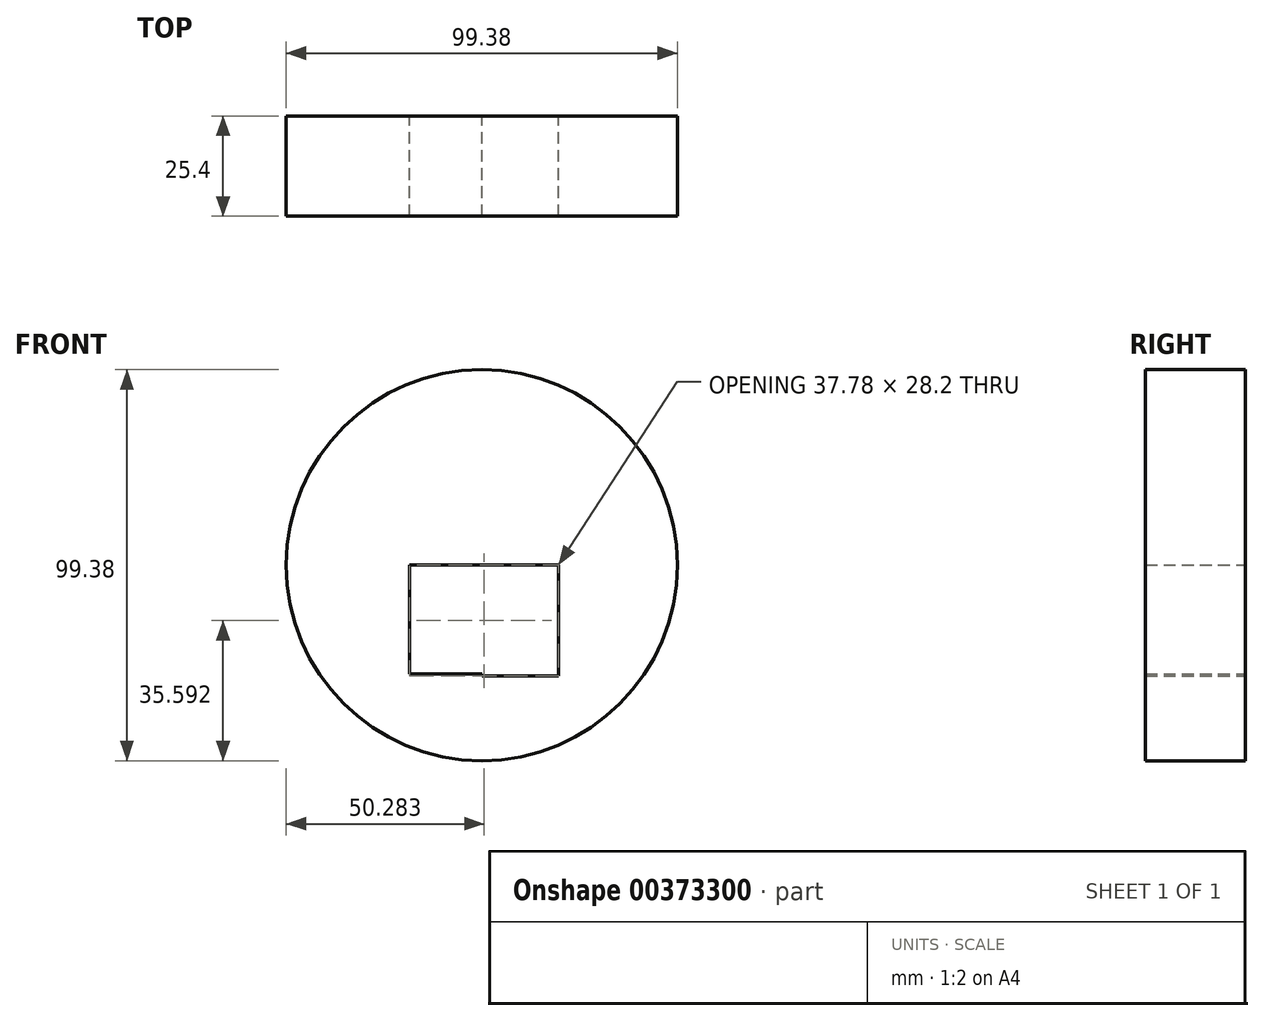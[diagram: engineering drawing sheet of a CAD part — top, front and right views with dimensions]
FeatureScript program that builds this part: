
annotation { "Feature Type Name" : "Feature", "Feature Type Description" : "" }
export const myFeature = defineFeature(function(context is Context, id is Id, definition is map)
    precondition{}
    {
        {
            var Q0;
            Q0=qCreatedBy(makeId("Front.planeOp"),FACE);
            var sketch = newSketch(context, id + "F0", { "sketchPlane" : qUnion([Q0])});
            skCircle(sketch, "E0", {"center": v(0, 0) * mm, "radius": 49.69 * mm});
            skLineSegment(sketch, "E1.bottom", {"start": v(0, 0) * mm, "end": v(19.48, 0) * mm});
            skLineSegment(sketch, "E1.top", {"start": v(0, -28.2) * mm, "end": v(19.48, -28.2) * mm});
            skLineSegment(sketch, "E1.left", {"start": v(0, 0) * mm, "end": v(0, -28.2) * mm});
            skLineSegment(sketch, "E1.right", {"start": v(19.48, 0) * mm, "end": v(19.48, -28.2) * mm});
            skLineSegment(sketch, "E2.bottom", {"start": v(0, 0) * mm, "end": v(-18.3, 0) * mm});
            skLineSegment(sketch, "E2.top", {"start": v(0, -27.65) * mm, "end": v(-18.3, -27.65) * mm});
            skLineSegment(sketch, "E2.left", {"start": v(0, 0) * mm, "end": v(0, -27.65) * mm});
            skLineSegment(sketch, "E2.right", {"start": v(-18.3, 0) * mm, "end": v(-18.3, -27.65) * mm});
            skSolve(sketch);
        }
        {
            var Q0;
            Q0 = qSketchRegion(id + "F0", true);
            extrude(context, id + "F1", {"entities" : qUnion([Q0]), "depth" : 25.4 * mm});
        }
    });
